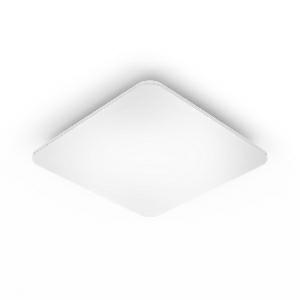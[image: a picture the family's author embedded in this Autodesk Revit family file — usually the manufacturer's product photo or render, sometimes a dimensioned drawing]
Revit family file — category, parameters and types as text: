
# Revit family: rs_pro_led_q1_007119
name_source: partatom
category: Leuchten
revit_build: Autodesk Revit 2016 (Build: 20190508_0715(x64)
units: mm (PartAtom-declared; Revit-internal decimal feet)

## family parameters
Basisbauteil = Fläche
Beim Laden mit Abzugskörper schneiden = Nein
Bemaßung runder Anschluss = Durchmesser verwenden
Gemeinsam genutzt = Nein
Lichtquelle = Nein
Raumberechnungspunkt = Nein
Teiletyp = Normal

## types (1)
- RS PRO LED Q1 (1 x , 2920 lm, 4000 K)
    Beschreibung = Dimensions (L x W x H): 56 x 331 x 331 mm; Mains power supply: 220 – 240 V / 50 – 60 Hz; Sensor Technology: High frequency; Transmitter power: < 1 mW; HF-system: 5,8 GHz; Output: 26 W; Interconnection: Yes; Type of interconnection: Master/master, Master/slave; Luminous flux: 2920 lm; Colour temperature: 4000 K; Colour variation LED: SDCM3; Colour Rendering Index CRI: 80-89; With lamp: Yes, STEINEL LED system; Lamp: LED cannot be replaced; LED life expectancy (max. °C): 50000 h; Drop in luminous flux in accordance with LM80: L70B10; Base: without; LED cooling system: Passive Thermo Control; With motion detector: Yes; Detection: also through glass, wood and stud walls; Detection angle: 360 °; Angle of aperture: 160 °; Capability of masking out individual segments: Yes; Electronic scalability: Yes; Mechanical scalability: No; Reach, radial: Ø 8 m (50 m²); Reach, tangential: Ø 8 m (50 m²); Main light adjustable: 50 - 100 %; Continuous light: selectable; Photo-cell controller: Yes; Twilight setting: 2 – 2000 lx; Time setting: 5 sec – 15 min; Basic light level function: Yes; Basic light level function time: 10/30 min, all night; Functions: Group parameterisation, Manual ON / ON-OFF, Master/slave override, Neighbouring-group function; Soft light start: Yes; Impact resistance: IK03; IP-rating: IP20; Protection class: II; Ambient temperature: -10 – 50 °C; Housing material: Aluminium; Cover material: Plastic, opal; Manufacturer's Warranty: 5 years; Settings via: DIP switches, Potentiometers, Remote control, Smart Remote; With remote control: No; Version: Neutral white white; PU1, EAN: 4007841007119
    CIE Flux Codes = 46 77 95 100 100
    Color Rendering = 80-89
    Color Temperature = 4000 K
    Frequency = 50 Hz, 60 Hz
    Height = 331 mm
    Hersteller = Steinel
    Lamp Light Flux = 2920 lm
    Lamp count = 1
    Lampe = 1 x
    Length = 56 mm  [stored 0.183727 ft]
    Luminous efficacy = 112 lm/W
    ModVariant = Nein
    Modell = 007119
    Mounting Type = Surface mounted
    Number of Poles = 1
    OnlyDefault = Ja
    Power Factor = 1
    Product Name = RS PRO LED Q1
    Product group = Sensor-switched indoor light
    ProductGroupID = 30
    Protection Class = Protection class II
    Protection Degree = IP 20
    RlxData = <blob elided: 27421 chars, md5=5dd89888>
    Scheinlast = 26 VA
    Socket = socket
    Standby Power = 0 W
    System Light Flux = 2920 lm
    System Power = 26 W
    Typenbild = produkt1_007119.jpg
    Typenkommentare = Product without accessories
    URL = http://relux.com
    VarID = ---
    Voltage = 0 V
    Vorgabe-Ansicht = 1800 mm
    Weight = 0.00 kg
    Width = 331 mm

note: [stored X ft] marks values corroborated as IEEE doubles in the binary element streams (Revit-internal decimal feet)

## geometry (parser evidence)
native form markers: Blend x4, Sweep x13
no freeform markers — native parametric forms only
